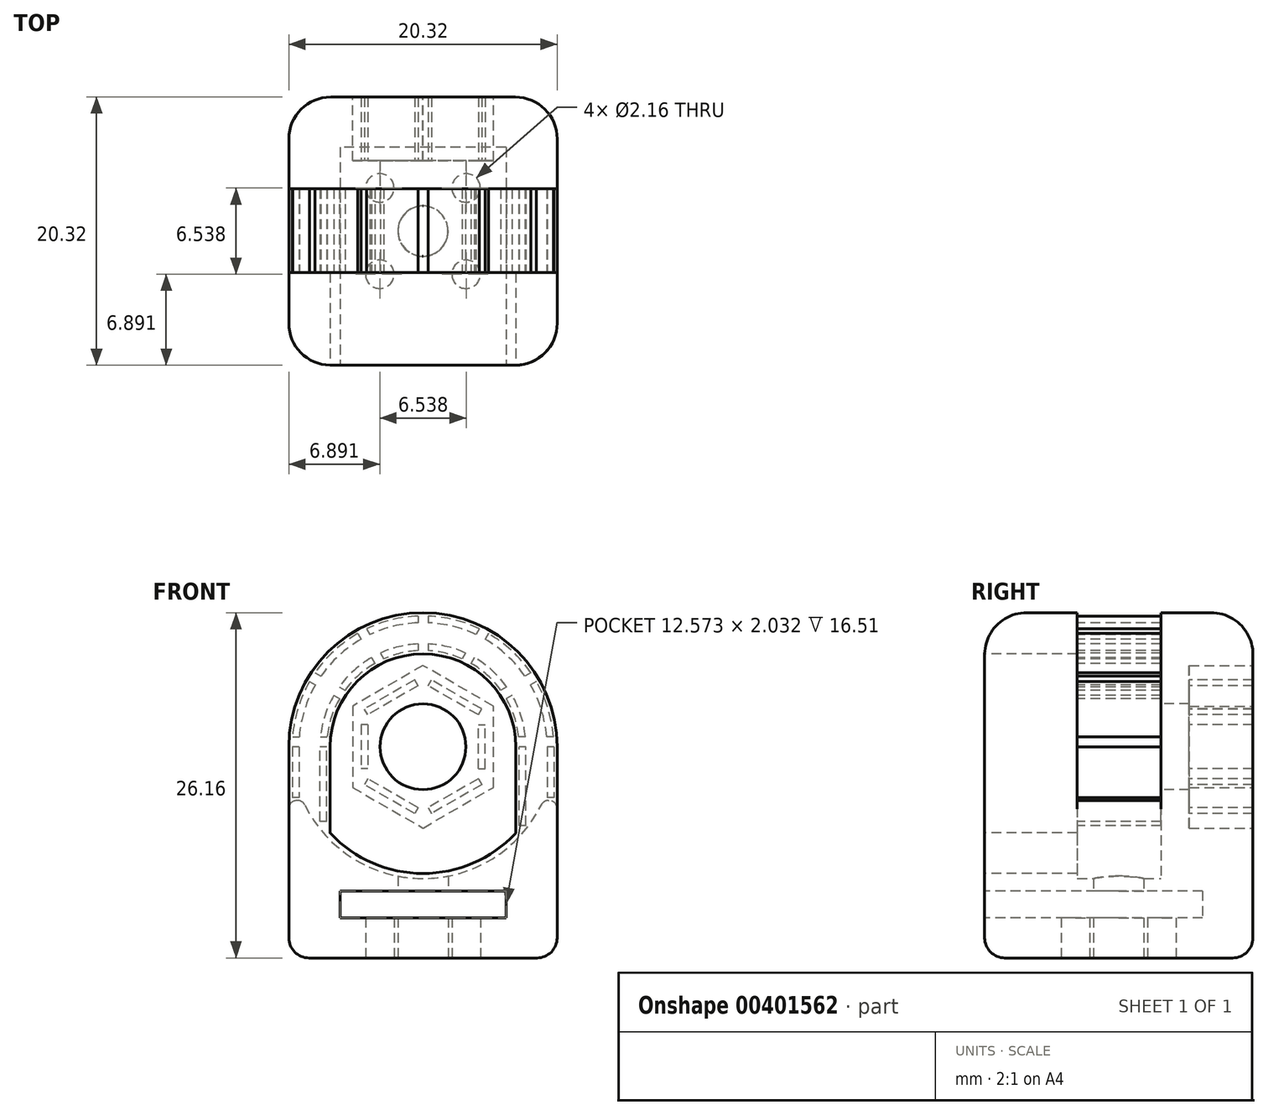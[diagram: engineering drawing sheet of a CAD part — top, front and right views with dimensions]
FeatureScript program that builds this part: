
annotation { "Feature Type Name" : "Feature", "Feature Type Description" : "" }
export const myFeature = defineFeature(function(context is Context, id is Id, definition is map)
    precondition{}
    {
        {
            var Q0;
            Q0=qCreatedBy(makeId("Top.planeOp"),FACE);
            var sketch = newSketch(context, id + "F0", { "sketchPlane" : qUnion([Q0])});
            skLineSegment(sketch, "E0.bottom", {"start": v(10.16, -10.16) * mm, "end": v(-10.16, -10.16) * mm});
            skLineSegment(sketch, "E0.top", {"start": v(10.16, 10.16) * mm, "end": v(-10.16, 10.16) * mm});
            skLineSegment(sketch, "E0.left", {"start": v(10.16, -10.16) * mm, "end": v(10.16, 10.16) * mm});
            skLineSegment(sketch, "E0.right", {"start": v(-10.16, -10.16) * mm, "end": v(-10.16, 10.16) * mm});
            skPoint(sketch, "E0.middle", {"position": v(0, 0) * mm});
            skSolve(sketch);
        }
        {
            var Q0;
            Q0=makeQuery(id+"F0.imprint","IMPRINT",FACE,{"disambiguationData":[TD([[makeQuery(id+"F0.imprint","IMPRINT",EDGE,{"derivedFrom":sQuery(id+"F0.wireOp",EDGE,"E0.bottom")}),-1.0]])]});
            extrude(context, id + "F1", {"entities" : qUnion([Q0]), "depth" : 26.16 * mm});
        }
        {
            var Q0;
            Q0=makeQuery(id+"F1.opExtrude","CAP_EDGE",EDGE,{"disambiguationData":[OSD([sQuery(id+"F0.wireOp",EDGE,"E0.left")])],"isStart":false});
            var Q1;
            Q1=makeQuery(id+"F1.opExtrude","CAP_EDGE",EDGE,{"disambiguationData":[OSD([sQuery(id+"F0.wireOp",EDGE,"E0.right")])],"isStart":false});
            fillet(context, id + "F2", {"entities" : qUnion([Q0, Q1]), "radius" : 10.16 * mm, "tangentPropagation" : true, "allowEdgeOverflow" : false});
        }
        {
            var Q0;
            Q0=makeQuery(id+"F1.opExtrude","SWEPT_FACE",FACE,{"disambiguationData":[OSD([sQuery(id+"F0.wireOp",EDGE,"E0.bottom")])]});
            var sketch = newSketch(context, id + "F3", { "sketchPlane" : qUnion([Q0])});
            skArc(sketch, "E1.0", {"start": v(10.16, 16) * mm, "mid": v(0, 26.16) * mm, "end": v(-10.16, 16) * mm, "construction": true});
            skCircle(sketch, "E2", {"center": v(0, 16) * mm, "radius": 3.25 * mm});
            skSolve(sketch);
        }
        {
            var Q0;
            Q0=makeQuery(id+"F3.imprint","IMPRINT",FACE,{"disambiguationData":[TD([[makeQuery(id+"F3.imprint","IMPRINT",EDGE,{"derivedFrom":sQuery(id+"F3.wireOp",EDGE,"E2")}),1.0]])]});
            extrude(context, id + "F4", {"entities" : qUnion([Q0]), "operationType" : NewBodyOperationType.REMOVE, "endBound" : BoundingType.THROUGH_ALL, "oppositeDirection" : true, "depth" : 25.4 * mm});
        }
        {
            var Q0;
            Q0=makeQuery(id+"F1.opExtrude","SWEPT_FACE",FACE,{"disambiguationData":[OSD([sQuery(id+"F0.wireOp",EDGE,"E0.bottom")])]});
            var sketch = newSketch(context, id + "F5", { "sketchPlane" : qUnion([Q0])});
            skCircle(sketch, "E3", {"center": v(0, 16) * mm, "radius": 9.6 * mm});
            skLineSegment(sketch, "E4", {"start": v(0, 0) * mm, "end": v(0, 7.09) * mm});
            skCircle(sketch, "E5", {"center": v(0, 16) * mm, "radius": 6.04 * mm});
            skSolve(sketch);
        }
        {
            var Q0;
            Q0=makeQuery(id+"F5.imprint","IMPRINT",FACE,{"disambiguationData":[TD([[makeQuery(id+"F5.imprint","IMPRINT",EDGE,{"derivedFrom":sQuery(id+"F5.wireOp",EDGE,"E3")}),-1.0]])]});
            var sketch = newSketch(context, id + "F6", { "sketchPlane" : qUnion([Q0])});
            skCircle(sketch, "E6.0", {"center": v(0, 16) * mm, "radius": 3.25 * mm, "construction": true});
            skCircle(sketch, "E7", {"center": v(0, 16) * mm, "radius": 3.14 * mm, "construction": true});
            skArc(sketch, "E8", {"start": v(6.93, 16) * mm, "mid": v(0, 22.94) * mm, "end": v(-6.93, 16) * mm, "construction": true});
            skLineSegment(sketch, "E9", {"start": v(-7.87, 6.43) * mm, "end": v(7.62, 6.43) * mm, "construction": true});
            skLineSegment(sketch, "E10", {"start": v(-10.79, 22.94) * mm, "end": v(12.96, 22.94) * mm, "construction": true});
            skArc(sketch, "E11", {"start": v(-6.93, 9.4) * mm, "mid": v(0, 6.43) * mm, "end": v(6.93, 9.4) * mm, "construction": true});
            skLineSegment(sketch, "E12", {"start": v(6.93, 16) * mm, "end": v(6.93, 9.4) * mm, "construction": true});
            skLineSegment(sketch, "E13", {"start": v(-6.93, 16) * mm, "end": v(-6.93, 9.4) * mm, "construction": true});
            skLineSegment(sketch, "E14.0", {"start": v(-7.04, 16) * mm, "end": v(-7.04, 9.36) * mm});
            skArc(sketch, "E14.1", {"start": v(7.04, 16) * mm, "mid": v(0, 23.04) * mm, "end": v(-7.04, 16) * mm});
            skLineSegment(sketch, "E14.2", {"start": v(7.04, 16) * mm, "end": v(7.04, 9.36) * mm});
            skArc(sketch, "E14.3", {"start": v(-7.04, 9.36) * mm, "mid": v(0, 6.32) * mm, "end": v(7.04, 9.36) * mm});
            skSolve(sketch);
        }
        {
            var Q0;
            {var subQ1=sQuery(id+"F6.wireOp",EDGE,"E14.1");Q0=makeQuery(id+"F6.imprint","IMPRINT",FACE,{"disambiguationData":[TD([[makeQuery(id+"F6.imprint","IMPRINT",EDGE,{"derivedFrom":subQ1}),1.0]])]});}
            extrude(context, id + "F7", {"entities" : qUnion([Q0]), "operationType" : NewBodyOperationType.REMOVE, "oppositeDirection" : true, "depth" : 13.36 * mm});
        }
        {
            var Q0;
            Q0=makeQuery(id+"F7.boolean.opBoolean","COPY",FACE,{"derivedFrom":makeQuery(id+"F7.opExtrude","CAP_FACE",FACE,{"disambiguationData":[OSD([sQuery(id+"F5.wireOp",EDGE,"E3"),sQuery(id+"F6.wireOp",EDGE,"E14.0"),sQuery(id+"F6.wireOp",EDGE,"E14.1"),sQuery(id+"F6.wireOp",EDGE,"E14.2")])],"isStart":false})});
            var sketch = newSketch(context, id + "F8", { "sketchPlane" : qUnion([Q0])});
            skArc(sketch, "E15.0", {"start": v(-6.93, 9.4) * mm, "mid": v(0, 6.43) * mm, "end": v(6.93, 9.4) * mm, "construction": true});
            skArc(sketch, "E16", {"start": v(-9.12, 11.94) * mm, "mid": v(0, 6.02) * mm, "end": v(9.12, 11.94) * mm});
            skLineSegment(sketch, "E17", {"start": v(-12.9, 11.94) * mm, "end": v(-9.12, 11.94) * mm});
            skLineSegment(sketch, "E18.trimOffspring", {"start": v(9.12, 11.94) * mm, "end": v(12.23, 11.94) * mm});
            skLineSegment(sketch, "E19", {"start": v(-12.9, 29.74) * mm, "end": v(12.23, 29.74) * mm});
            skLineSegment(sketch, "E20", {"start": v(12.23, 29.74) * mm, "end": v(12.23, 11.94) * mm});
            skLineSegment(sketch, "E21", {"start": v(-12.9, 29.74) * mm, "end": v(-12.9, 11.94) * mm});
            skSolve(sketch);
        }
        {
            var Q0;
            Q0=makeQuery(id+"F8.imprint","IMPRINT",FACE,{"disambiguationData":[TD([[makeQuery(id+"F8.imprint","IMPRINT",EDGE,{"derivedFrom":sQuery(id+"F8.wireOp",EDGE,"E16")}),1.0]])]});
            extrude(context, id + "F9", {"entities" : qUnion([Q0]), "operationType" : NewBodyOperationType.REMOVE, "depth" : 6.35 * mm});
        }
        {
            var Q0;
            Q0=makeQuery(id+"F9.boolean.opBoolean","COPY",EDGE,{"derivedFrom":makeQuery(id+"F9.opExtrude","SWEPT_EDGE",EDGE,{"disambiguationData":[OSD([sQuery(id+"F8.wireOp",EDGE,"E16"),sQuery(id+"F8.wireOp",EDGE,"E18.trimOffspring")])]})});
            var Q1;
            Q1=makeQuery(id+"F9.boolean.opBoolean","INTERSECT",EDGE,{"derivedFrom":[makeQuery(id+"F1.opExtrude","SWEPT_FACE",FACE,{"disambiguationData":[OSD([sQuery(id+"F0.wireOp",EDGE,"E0.left")])]}),makeQuery(id+"F9.opExtrude","SWEPT_FACE",FACE,{"disambiguationData":[OSD([sQuery(id+"F8.wireOp",EDGE,"E18.trimOffspring")])]})]});
            var Q2;
            Q2=makeQuery(id+"F9.boolean.opBoolean","COPY",EDGE,{"derivedFrom":makeQuery(id+"F9.opExtrude","SWEPT_EDGE",EDGE,{"disambiguationData":[OSD([sQuery(id+"F8.wireOp",EDGE,"E16"),sQuery(id+"F8.wireOp",EDGE,"E17")])]})});
            var Q3;
            Q3=makeQuery(id+"F9.boolean.opBoolean","INTERSECT",EDGE,{"derivedFrom":[makeQuery(id+"F1.opExtrude","SWEPT_FACE",FACE,{"disambiguationData":[OSD([sQuery(id+"F0.wireOp",EDGE,"E0.right")])]}),makeQuery(id+"F9.opExtrude","SWEPT_FACE",FACE,{"disambiguationData":[OSD([sQuery(id+"F8.wireOp",EDGE,"E17")])]})]});
            fillet(context, id + "F10", {"entities" : qUnion([Q0, Q1, Q2, Q3]), "radius" : 0.64 * mm, "tangentPropagation" : true, "allowEdgeOverflow" : false});
        }
        {
            var Q0;
            Q0=makeQuery(id+"F1.opExtrude","SWEPT_FACE",FACE,{"disambiguationData":[OSD([sQuery(id+"F0.wireOp",EDGE,"E0.top")])]});
            var sketch = newSketch(context, id + "F11", { "sketchPlane" : qUnion([Q0])});
            skLineSegment(sketch, "E22", {"start": v(0, 16) * mm, "end": v(-24.5, 16) * mm, "construction": true});
            skCircle(sketch, "E23.cCircle", {"center": v(0, 16) * mm, "radius": 5.33 * mm, "construction": true});
            skLineSegment(sketch, "E23.0", {"start": v(5.33, 12.92) * mm, "end": v(0, 9.84) * mm});
            skLineSegment(sketch, "E23.1", {"start": v(0, 9.84) * mm, "end": v(-5.34, 12.92) * mm});
            skLineSegment(sketch, "E23.2", {"start": v(-5.34, 12.92) * mm, "end": v(-5.33, 19.08) * mm});
            skLineSegment(sketch, "E23.3", {"start": v(-5.33, 19.08) * mm, "end": v(0, 22.16) * mm});
            skLineSegment(sketch, "E23.4", {"start": v(0, 22.16) * mm, "end": v(5.34, 19.08) * mm});
            skLineSegment(sketch, "E23.5", {"start": v(5.34, 19.08) * mm, "end": v(5.33, 12.92) * mm});
            skPoint(sketch, "E23.0.midPoint", {"position": v(2.66, 11.38) * mm});
            skSolve(sketch);
        }
        {
            var Q0;
            Q0=makeQuery(id+"F11.imprint","IMPRINT",FACE,{"disambiguationData":[TD([[makeQuery(id+"F11.imprint","IMPRINT",EDGE,{"derivedFrom":sQuery(id+"F11.wireOp",EDGE,"E23.0")}),-1.0]])]});
            extrude(context, id + "F12", {"entities" : qUnion([Q0]), "operationType" : NewBodyOperationType.REMOVE, "oppositeDirection" : true, "depth" : 4.83 * mm});
        }
        {
            var Q0;
            Q0=makeQuery(id+"F1.opExtrude","CAP_FACE",FACE,{"disambiguationData":[OSD([sQuery(id+"F0.wireOp",EDGE,"E0.bottom"),sQuery(id+"F0.wireOp",EDGE,"E0.top"),sQuery(id+"F0.wireOp",EDGE,"E0.left"),sQuery(id+"F0.wireOp",EDGE,"E0.right")])],"isStart":true});
            var sketch = newSketch(context, id + "F13", { "sketchPlane" : qUnion([Q0])});
            skCircle(sketch, "E24", {"center": v(0, 0) * mm, "radius": 1.9 * mm});
            skSolve(sketch);
        }
        {
            var Q0;
            Q0 = qSketchRegion(id + "F13", true);
            extrude(context, id + "F14", {"entities" : qUnion([Q0]), "operationType" : NewBodyOperationType.REMOVE, "oppositeDirection" : true, "depth" : 25.4 * mm});
        }
        {
            var Q0;
            Q0=makeQuery(id+"F1.opExtrude","CAP_FACE",FACE,{"disambiguationData":[OSD([sQuery(id+"F0.wireOp",EDGE,"E0.bottom"),sQuery(id+"F0.wireOp",EDGE,"E0.top"),sQuery(id+"F0.wireOp",EDGE,"E0.left"),sQuery(id+"F0.wireOp",EDGE,"E0.right")])],"isStart":true});
            var sketch = newSketch(context, id + "F15", { "sketchPlane" : qUnion([Q0])});
            skSolve(sketch);
        }
        {
            var Q0;
            Q0=makeQuery(id+"F1.opExtrude","SWEPT_FACE",FACE,{"disambiguationData":[OSD([sQuery(id+"F0.wireOp",EDGE,"E0.bottom")])]});
            var sketch = newSketch(context, id + "F16", { "sketchPlane" : qUnion([Q0])});
            skLineSegment(sketch, "E25", {"start": v(6.29, 3.05) * mm, "end": v(-6.29, 3.05) * mm});
            skLineSegment(sketch, "E26", {"start": v(6.29, 5.08) * mm, "end": v(-6.29, 5.08) * mm});
            skLineSegment(sketch, "E27", {"start": v(-6.29, 5.08) * mm, "end": v(-6.29, 3.05) * mm});
            skLineSegment(sketch, "E28", {"start": v(6.29, 5.08) * mm, "end": v(6.29, 3.05) * mm});
            skLineSegment(sketch, "E29", {"start": v(0, 13.37) * mm, "end": v(0, -3.67) * mm, "construction": true});
            skPoint(sketch, "E29.endSnap0", {"position": v(0, 6.43) * mm});
            skSolve(sketch);
        }
        {
            var Q0;
            Q0=makeQuery(id+"F16.imprint","IMPRINT",FACE,{"disambiguationData":[TD([[makeQuery(id+"F16.imprint","IMPRINT",EDGE,{"derivedFrom":sQuery(id+"F16.wireOp",EDGE,"E25")}),-1.0]])]});
            extrude(context, id + "F17", {"entities" : qUnion([Q0]), "operationType" : NewBodyOperationType.REMOVE, "oppositeDirection" : true, "depth" : 16.5 * mm});
        }
        {
            var Q0;
            Q0=makeQuery(id+"F15.imprint","IMPRINT",FACE,{"disambiguationData":[TD([[makeQuery(id+"F15.imprint","IMPRINT",EDGE,{"derivedFrom":makeQuery(id+"F1.opExtrude","CAP_EDGE",EDGE,{"disambiguationData":[OSD([sQuery(id+"F0.wireOp",EDGE,"E0.bottom")])],"isStart":true})}),1.0]])]});
            var sketch = newSketch(context, id + "F18", { "sketchPlane" : qUnion([Q0])});
            skCircle(sketch, "E30", {"center": v(0, 0) * mm, "radius": 4.62 * mm, "construction": true});
            skLineSegment(sketch, "E31", {"start": v(0, 0) * mm, "end": v(15.47, 0) * mm, "construction": true});
            skLineSegment(sketch, "E32", {"start": v(0, 0) * mm, "end": v(3.27, 3.27) * mm, "construction": true});
            skCircle(sketch, "E33", {"center": v(3.27, 3.27) * mm, "radius": 1.08 * mm});
            skCircle(sketch, "E34.1.0", {"center": v(-3.27, 3.27) * mm, "radius": 1.08 * mm});
            skCircle(sketch, "E34.2.0", {"center": v(-3.27, -3.27) * mm, "radius": 1.08 * mm});
            skCircle(sketch, "E34.3.0", {"center": v(3.27, -3.27) * mm, "radius": 1.08 * mm});
            skSolve(sketch);
        }
        {
            var Q0;
            Q0 = qSketchRegion(id + "F18", true);
            var Q1;
            Q1=makeQuery(id+"F17.boolean.opBoolean","COPY",FACE,{"derivedFrom":makeQuery(id+"F17.opExtrude","SWEPT_FACE",FACE,{"disambiguationData":[OSD([sQuery(id+"F16.wireOp",EDGE,"E26")])]})});
            extrude(context, id + "F19", {"entities" : qUnion([Q0]), "operationType" : NewBodyOperationType.REMOVE, "endBound" : BoundingType.UP_TO_SURFACE, "oppositeDirection" : true, "endBoundEntityFace" : qUnion([Q1]), "depth" : 25.4 * mm});
        }
        {
            var Q0;
            Q0=makeQuery(id+"F2.opFillet","BLEND_EDGE",EDGE,{"blendedFrom":[makeQuery(id+"F1.opExtrude","CAP_EDGE",EDGE,{"disambiguationData":[OSD([sQuery(id+"F0.wireOp",EDGE,"E0.left")])],"isStart":false}),makeQuery(id+"F1.opExtrude","SWEPT_FACE",FACE,{"disambiguationData":[OSD([sQuery(id+"F0.wireOp",EDGE,"E0.bottom")])]})],"blendedInto":[makeQuery(id+"F1.opExtrude","SWEPT_FACE",FACE,{"disambiguationData":[OSD([sQuery(id+"F0.wireOp",EDGE,"E0.bottom")])]})]});
            var Q1;
            Q1=makeQuery(id+"F1.opExtrude","SWEPT_EDGE",EDGE,{"disambiguationData":[OSD([sQuery(id+"F0.wireOp",EDGE,"E0.top"),sQuery(id+"F0.wireOp",EDGE,"E0.right")])]});
            fillet(context, id + "F20", {"entities" : qUnion([Q0, Q1]), "radius" : 3.17 * mm, "tangentPropagation" : true, "allowEdgeOverflow" : false});
        }
        {
            var Q0;
            Q0=makeQuery(id+"F1.opExtrude","CAP_EDGE",EDGE,{"disambiguationData":[OSD([sQuery(id+"F0.wireOp",EDGE,"E0.left")])],"isStart":true});
            fillet(context, id + "F21", {"entities" : qUnion([Q0]), "radius" : 1.52 * mm, "tangentPropagation" : true, "allowEdgeOverflow" : false});
        }
        {
            var Q0;
            Q0=makeQuery(id+"F9.boolean.opBoolean","COPY",FACE,{"derivedFrom":makeQuery(id+"F9.opExtrude","CAP_FACE",FACE,{"disambiguationData":[OSD([sQuery(id+"F5.wireOp",EDGE,"E3"),sQuery(id+"F6.wireOp",EDGE,"E14.0"),sQuery(id+"F6.wireOp",EDGE,"E14.1"),sQuery(id+"F6.wireOp",EDGE,"E14.2"),sQuery(id+"F8.wireOp",EDGE,"E16"),sQuery(id+"F8.wireOp",EDGE,"E17"),sQuery(id+"F8.wireOp",EDGE,"E18.trimOffspring"),sQuery(id+"F8.wireOp",EDGE,"E19"),sQuery(id+"F8.wireOp",EDGE,"E20"),sQuery(id+"F8.wireOp",EDGE,"E21")])],"isStart":false})});
            var sketch = newSketch(context, id + "F22", { "sketchPlane" : qUnion([Q0])});
            skArc(sketch, "E35.0", {"start": v(9.88, 16.76) * mm, "mid": v(9.46, 18.93) * mm, "end": v(8.58, 20.96) * mm});
            skLineSegment(sketch, "E36.0", {"start": v(-9.9, 12.16) * mm, "end": v(-9.9, 16) * mm});
            skLineSegment(sketch, "E37.0", {"start": v(9.9, 12.16) * mm, "end": v(9.9, 16) * mm});
            skLineSegment(sketch, "E38.0", {"start": v(-9.4, 12.16) * mm, "end": v(-9.4, 16) * mm});
            skArc(sketch, "E38.1", {"start": v(9.37, 16.76) * mm, "mid": v(8.97, 18.8) * mm, "end": v(8.14, 20.7) * mm});
            skLineSegment(sketch, "E38.2", {"start": v(9.4, 12.16) * mm, "end": v(9.4, 16) * mm});
            skLineSegment(sketch, "E39.0", {"start": v(7.29, 16) * mm, "end": v(7.29, 10.35) * mm});
            skArc(sketch, "E39.1", {"start": v(-7.25, 16.76) * mm, "mid": v(-6.93, 18.25) * mm, "end": v(-6.31, 19.65) * mm});
            skLineSegment(sketch, "E39.2", {"start": v(-7.29, 16) * mm, "end": v(-7.29, 10.03) * mm});
            skLineSegment(sketch, "E40.0", {"start": v(7.8, 16) * mm, "end": v(7.8, 10.35) * mm});
            skArc(sketch, "E40.1", {"start": v(-7.76, 16.76) * mm, "mid": v(-7.42, 18.39) * mm, "end": v(-6.75, 19.9) * mm});
            skLineSegment(sketch, "E40.2", {"start": v(-7.8, 16) * mm, "end": v(-7.8, 10.02) * mm});
            skLineSegment(sketch, "E41", {"start": v(9.9, 12.16) * mm, "end": v(9.4, 12.16) * mm});
            skLineSegment(sketch, "E42", {"start": v(7.8, 10.35) * mm, "end": v(7.29, 10.35) * mm});
            skLineSegment(sketch, "E43", {"start": v(-7.29, 10.03) * mm, "end": v(-7.8, 10.02) * mm});
            skLineSegment(sketch, "E44.trimOffspring", {"start": v(-9.4, 12.16) * mm, "end": v(-9.9, 12.16) * mm});
            skLineSegment(sketch, "E45", {"start": v(9.9, 16) * mm, "end": v(9.4, 16) * mm});
            skLineSegment(sketch, "E46", {"start": v(7.8, 16) * mm, "end": v(7.29, 16) * mm});
            skLineSegment(sketch, "E47", {"start": v(-7.29, 16) * mm, "end": v(-7.8, 16) * mm});
            skLineSegment(sketch, "E48", {"start": v(-9.4, 16) * mm, "end": v(-9.9, 16) * mm});
            skLineSegment(sketch, "E49.0", {"start": v(7.25, 16.76) * mm, "end": v(7.76, 16.76) * mm});
            skLineSegment(sketch, "E50.trimOffspring", {"start": v(9.37, 16.76) * mm, "end": v(9.88, 16.76) * mm});
            skLineSegment(sketch, "E51.0", {"start": v(-9.37, 16.76) * mm, "end": v(-9.88, 16.76) * mm});
            skLineSegment(sketch, "E52.0", {"start": v(-7.25, 16.76) * mm, "end": v(-7.8, 16.76) * mm});
            skLineSegment(sketch, "E53", {"start": v(0, 22.2) * mm, "end": v(0, 26.73) * mm, "construction": true});
            skPoint(sketch, "E53.endSnap0", {"position": v(0, 25.9) * mm});
            skLineSegment(sketch, "E54.0", {"start": v(0.38, 23.28) * mm, "end": v(0.38, 23.8) * mm});
            skLineSegment(sketch, "E55.0", {"start": v(-0.38, 23.28) * mm, "end": v(-0.38, 23.8) * mm});
            skArc(sketch, "E56.trimOffspring", {"start": v(0.38, 23.28) * mm, "mid": v(1.7, 23.1) * mm, "end": v(2.97, 22.66) * mm});
            skArc(sketch, "E57.trimOffspring", {"start": v(0.38, 23.8) * mm, "mid": v(1.83, 23.58) * mm, "end": v(3.22, 23.1) * mm});
            skArc(sketch, "E58.trimOffspring", {"start": v(-0.38, 25.4) * mm, "mid": v(-2.25, 25.13) * mm, "end": v(-4.02, 24.5) * mm});
            skArc(sketch, "E59.trimOffspring", {"start": v(0, 25.9) * mm, "mid": v(-2.2, 25.66) * mm, "end": v(-4.28, 24.94) * mm});
            skLineSegment(sketch, "E60.trimOffspring", {"start": v(0.38, 25.4) * mm, "end": v(0.38, 25.9) * mm});
            skLineSegment(sketch, "E61.trimOffspring", {"start": v(-0.38, 25.4) * mm, "end": v(-0.38, 25.9) * mm});
            skLineSegment(sketch, "E62", {"start": v(6.31, 19.65) * mm, "end": v(6.75, 19.9) * mm});
            skLineSegment(sketch, "E63", {"start": v(0, 16) * mm, "end": v(0.76, 17.32) * mm});
            skLineSegment(sketch, "E64.0", {"start": v(-0.38, 16.66) * mm, "end": v(0.76, 17.32) * mm});
            skLineSegment(sketch, "E65.0", {"start": v(2.97, 22.66) * mm, "end": v(3.22, 23.1) * mm});
            skArc(sketch, "E66.trimOffspring", {"start": v(6.31, 19.65) * mm, "mid": v(6.93, 18.25) * mm, "end": v(7.25, 16.76) * mm});
            skArc(sketch, "E67.trimOffspring", {"start": v(6.75, 19.9) * mm, "mid": v(7.42, 18.39) * mm, "end": v(7.76, 16.76) * mm});
            skArc(sketch, "E68.trimOffspring", {"start": v(7.73, 21.35) * mm, "mid": v(6.37, 22.91) * mm, "end": v(4.7, 24.14) * mm});
            skArc(sketch, "E69.trimOffspring", {"start": v(8.17, 21.6) * mm, "mid": v(6.73, 23.27) * mm, "end": v(4.95, 24.58) * mm});
            skLineSegment(sketch, "E70.trimOffspring", {"start": v(8.14, 20.7) * mm, "end": v(8.58, 20.96) * mm});
            skLineSegment(sketch, "E71.trimOffspring", {"start": v(7.73, 21.35) * mm, "end": v(8.2, 21.61) * mm});
            skLineSegment(sketch, "E72.trimOffspring", {"start": v(5.9, 20.29) * mm, "end": v(6.34, 20.54) * mm});
            skLineSegment(sketch, "E73.trimOffspring", {"start": v(4.7, 24.14) * mm, "end": v(4.95, 24.58) * mm});
            skLineSegment(sketch, "E74.trimOffspring", {"start": v(4.02, 24.5) * mm, "end": v(4.3, 24.96) * mm});
            skArc(sketch, "E75.trimOffspring", {"start": v(3.64, 22.32) * mm, "mid": v(4.88, 21.42) * mm, "end": v(5.9, 20.29) * mm});
            skArc(sketch, "E76.trimOffspring", {"start": v(3.9, 22.76) * mm, "mid": v(5.24, 21.78) * mm, "end": v(6.34, 20.54) * mm});
            skArc(sketch, "E77.trimOffspring", {"start": v(4.02, 24.5) * mm, "mid": v(2.25, 25.13) * mm, "end": v(0.38, 25.4) * mm});
            skArc(sketch, "E78.trimOffspring", {"start": v(4.28, 24.94) * mm, "mid": v(2.38, 25.62) * mm, "end": v(0.38, 25.9) * mm});
            skLineSegment(sketch, "E79.trimOffspring", {"start": v(3.64, 22.32) * mm, "end": v(3.9, 22.76) * mm});
            skLineSegment(sketch, "E80.MirrorCS", {"start": v(-4.02, 24.5) * mm, "end": v(-4.3, 24.96) * mm});
            skLineSegment(sketch, "E81.MirrorCS", {"start": v(-2.97, 22.66) * mm, "end": v(-3.22, 23.1) * mm});
            skLineSegment(sketch, "E82.MirrorCS", {"start": v(-3.64, 22.32) * mm, "end": v(-3.9, 22.76) * mm});
            skLineSegment(sketch, "E83.MirrorCS", {"start": v(-4.7, 24.14) * mm, "end": v(-4.95, 24.58) * mm});
            skLineSegment(sketch, "E84.MirrorCS", {"start": v(-8.14, 20.7) * mm, "end": v(-8.58, 20.96) * mm});
            skLineSegment(sketch, "E85.MirrorCS", {"start": v(-6.31, 19.65) * mm, "end": v(-6.75, 19.9) * mm});
            skLineSegment(sketch, "E86.MirrorCS", {"start": v(-5.9, 20.29) * mm, "end": v(-6.34, 20.54) * mm});
            skArc(sketch, "E87.trimOffspring", {"start": v(-4.95, 24.58) * mm, "mid": v(-6.73, 23.27) * mm, "end": v(-8.17, 21.6) * mm});
            skArc(sketch, "E88.trimOffspring", {"start": v(-4.7, 24.14) * mm, "mid": v(-6.37, 22.91) * mm, "end": v(-7.73, 21.35) * mm});
            skArc(sketch, "E89.trimOffspring", {"start": v(-3.22, 23.1) * mm, "mid": v(-1.83, 23.58) * mm, "end": v(-0.38, 23.8) * mm});
            skArc(sketch, "E90.trimOffspring", {"start": v(-2.97, 22.66) * mm, "mid": v(-1.7, 23.1) * mm, "end": v(-0.38, 23.28) * mm});
            skArc(sketch, "E91.trimOffspring", {"start": v(-6.34, 20.54) * mm, "mid": v(-5.24, 21.78) * mm, "end": v(-3.9, 22.76) * mm});
            skArc(sketch, "E92.trimOffspring", {"start": v(-5.9, 20.29) * mm, "mid": v(-4.88, 21.42) * mm, "end": v(-3.64, 22.32) * mm});
            skLineSegment(sketch, "E93.MirrorCS", {"start": v(-7.73, 21.35) * mm, "end": v(-8.2, 21.61) * mm});
            skArc(sketch, "E94.trimOffspring", {"start": v(-8.58, 20.96) * mm, "mid": v(-9.46, 18.93) * mm, "end": v(-9.88, 16.76) * mm});
            skArc(sketch, "E95.trimOffspring", {"start": v(-8.14, 20.7) * mm, "mid": v(-8.97, 18.8) * mm, "end": v(-9.37, 16.76) * mm});
            skSolve(sketch);
        }
        {
            var Q0;
            Q0 = qSketchRegion(id + "F22", true);
            var Q1;
            {var subQ0=sQuery(id+"F6.wireOp",EDGE,"E14.2");var subQ1=sQuery(id+"F6.wireOp",EDGE,"E14.1");var subQ2=sQuery(id+"F6.wireOp",EDGE,"E14.0");var subQ3=sQuery(id+"F5.wireOp",EDGE,"E3");Q1=makeQuery(id+"F9.boolean.opBoolean","MERGE",FACE,{"derivedFrom":[makeQuery(id+"F7.boolean.opBoolean","COPY",FACE,{"derivedFrom":makeQuery(id+"F7.opExtrude","CAP_FACE",FACE,{"disambiguationData":[OSD([subQ3,subQ2,subQ1,subQ0])],"isStart":false})}),makeQuery(id+"F9.opExtrude","CAP_FACE",FACE,{"disambiguationData":[OSD([subQ3,subQ2,subQ1,subQ0,sQuery(id+"F8.wireOp",EDGE,"E16"),sQuery(id+"F8.wireOp",EDGE,"E17"),sQuery(id+"F8.wireOp",EDGE,"E18.trimOffspring"),sQuery(id+"F8.wireOp",EDGE,"E19"),sQuery(id+"F8.wireOp",EDGE,"E20"),sQuery(id+"F8.wireOp",EDGE,"E21")])],"isStart":true})]});}
            extrude(context, id + "F23", {"entities" : qUnion([Q0]), "operationType" : NewBodyOperationType.ADD, "endBound" : BoundingType.UP_TO_SURFACE, "endBoundEntityFace" : qUnion([Q1]), "depth" : 25.4 * mm});
        }
        {
            var Q0;
            Q0=makeQuery(id+"F12.boolean.opBoolean","COPY",FACE,{"derivedFrom":makeQuery(id+"F12.opExtrude","CAP_FACE",FACE,{"disambiguationData":[OSD([sQuery(id+"F0.wireOp",EDGE,"E0.top"),sQuery(id+"F3.wireOp",EDGE,"E2"),sQuery(id+"F11.wireOp",EDGE,"E23.0"),sQuery(id+"F11.wireOp",EDGE,"E23.1"),sQuery(id+"F11.wireOp",EDGE,"E23.2"),sQuery(id+"F11.wireOp",EDGE,"E23.3"),sQuery(id+"F11.wireOp",EDGE,"E23.4"),sQuery(id+"F11.wireOp",EDGE,"E23.5")])],"isStart":false})});
            var sketch = newSketch(context, id + "F24", { "sketchPlane" : qUnion([Q0])});
            skLineSegment(sketch, "E96.0", {"start": v(-4.44, 18.86) * mm, "end": v(-0.64, 21.06) * mm});
            skLineSegment(sketch, "E96.1", {"start": v(4.7, 17.66) * mm, "end": v(4.7, 14.34) * mm});
            skLineSegment(sketch, "E96.3", {"start": v(0.63, 21.06) * mm, "end": v(4.44, 18.86) * mm});
            skLineSegment(sketch, "E96.5", {"start": v(-4.7, 14.34) * mm, "end": v(-4.7, 17.66) * mm});
            skLineSegment(sketch, "E97.0", {"start": v(-4.19, 18.42) * mm, "end": v(-0.38, 20.62) * mm});
            skLineSegment(sketch, "E97.1", {"start": v(4.2, 17.66) * mm, "end": v(4.2, 14.34) * mm});
            skLineSegment(sketch, "E97.3", {"start": v(0.38, 20.62) * mm, "end": v(4.2, 18.42) * mm});
            skLineSegment(sketch, "E97.5", {"start": v(-4.2, 14.34) * mm, "end": v(-4.2, 17.66) * mm});
            skLineSegment(sketch, "E98.0", {"start": v(4.2, 14.34) * mm, "end": v(4.7, 14.34) * mm});
            skLineSegment(sketch, "E99", {"start": v(0, 16) * mm, "end": v(-1.64, 16) * mm, "construction": true});
            skLineSegment(sketch, "E100", {"start": v(0, 16) * mm, "end": v(0, 17.47) * mm, "construction": true});
            skLineSegment(sketch, "E101.MirrorCS", {"start": v(4.2, 17.66) * mm, "end": v(4.7, 17.66) * mm});
            skLineSegment(sketch, "E102.MirrorCS", {"start": v(-4.19, 18.42) * mm, "end": v(-4.44, 18.86) * mm});
            skLineSegment(sketch, "E103.MirrorCS", {"start": v(-4.2, 17.66) * mm, "end": v(-4.7, 17.66) * mm});
            skLineSegment(sketch, "E104.MirrorCS", {"start": v(-4.2, 14.34) * mm, "end": v(-4.7, 14.34) * mm});
            skPoint(sketch, "E105.orphan", {"position": v(4.7, 17.66) * mm});
            skPoint(sketch, "E106.orphan", {"position": v(-4.7, 17.66) * mm});
            skPoint(sketch, "E107.orphan", {"position": v(-4.7, 14.34) * mm});
            skLineSegment(sketch, "E108", {"start": v(0.38, 20.62) * mm, "end": v(0.63, 21.06) * mm});
            skLineSegment(sketch, "E109", {"start": v(-0.38, 20.62) * mm, "end": v(-0.64, 21.06) * mm});
            skLineSegment(sketch, "E110", {"start": v(4.2, 18.42) * mm, "end": v(4.44, 18.86) * mm});
            skLineSegment(sketch, "E111.MirrorCS", {"start": v(-4.19, 13.58) * mm, "end": v(-4.44, 13.14) * mm});
            skLineSegment(sketch, "E112.MirrorCS", {"start": v(4.2, 13.58) * mm, "end": v(4.44, 13.14) * mm});
            skLineSegment(sketch, "E113.MirrorCS", {"start": v(0.38, 11.38) * mm, "end": v(0.63, 10.94) * mm});
            skLineSegment(sketch, "E114.MirrorCS", {"start": v(-0.38, 11.38) * mm, "end": v(-0.64, 10.94) * mm});
            skLineSegment(sketch, "E115.MirrorCS", {"start": v(-4.19, 13.58) * mm, "end": v(-0.38, 11.38) * mm});
            skLineSegment(sketch, "E116.MirrorCS", {"start": v(0.63, 10.94) * mm, "end": v(4.44, 13.14) * mm});
            skLineSegment(sketch, "E117.MirrorCS", {"start": v(-4.44, 13.14) * mm, "end": v(-0.64, 10.94) * mm});
            skLineSegment(sketch, "E118.MirrorCS", {"start": v(0.38, 11.38) * mm, "end": v(4.2, 13.58) * mm});
            skSolve(sketch);
        }
        {
            var Q0;
            Q0 = qSketchRegion(id + "F24", true);
            var Q1;
            Q1=makeQuery(id+"F1.opExtrude","SWEPT_FACE",FACE,{"disambiguationData":[OSD([sQuery(id+"F0.wireOp",EDGE,"E0.top")])]});
            extrude(context, id + "F25", {"entities" : qUnion([Q0]), "operationType" : NewBodyOperationType.ADD, "endBound" : BoundingType.UP_TO_SURFACE, "endBoundEntityFace" : qUnion([Q1]), "depth" : 25.4 * mm});
        }
    });
